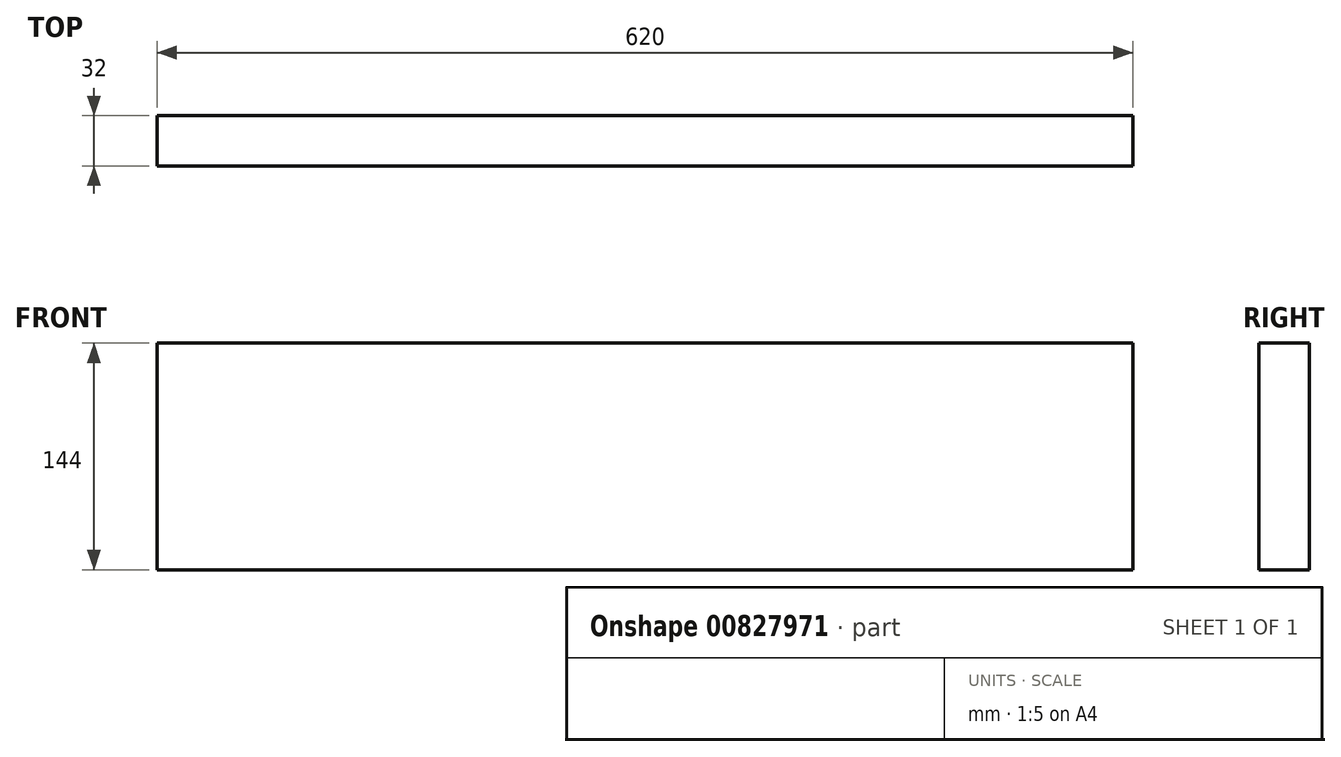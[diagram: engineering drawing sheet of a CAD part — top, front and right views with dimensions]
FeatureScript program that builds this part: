
annotation { "Feature Type Name" : "Feature", "Feature Type Description" : "" }
export const myFeature = defineFeature(function(context is Context, id is Id, definition is map)
    precondition{}
    {
        {
            var Q0;
            Q0=qCreatedBy(makeId("Top.planeOp"),FACE);
            var sketch = newSketch(context, id + "F0", { "sketchPlane" : qUnion([Q0])});
            skLineSegment(sketch, "E0.bottom", {"start": v(-310, 16) * mm, "end": v(310, 16) * mm});
            skLineSegment(sketch, "E0.top", {"start": v(-310, -16) * mm, "end": v(310, -16) * mm});
            skLineSegment(sketch, "E0.left", {"start": v(-310, 16) * mm, "end": v(-310, -16) * mm});
            skLineSegment(sketch, "E0.right", {"start": v(310, 16) * mm, "end": v(310, -16) * mm});
            skPoint(sketch, "E0.middle", {"position": v(0, 0) * mm});
            skSolve(sketch);
        }
        {
            var Q0;
            Q0=makeQuery(id+"F0.imprint","IMPRINT",FACE,{"disambiguationData":[TD([[makeQuery(id+"F0.imprint","IMPRINT",EDGE,{"derivedFrom":sQuery(id+"F0.wireOp",EDGE,"E0.bottom")}),-1.0]])]});
            extrude(context, id + "F1", {"entities" : qUnion([Q0]), "depth" : 144 * mm, "offsetDistance" : 25 * mm});
        }
    });
